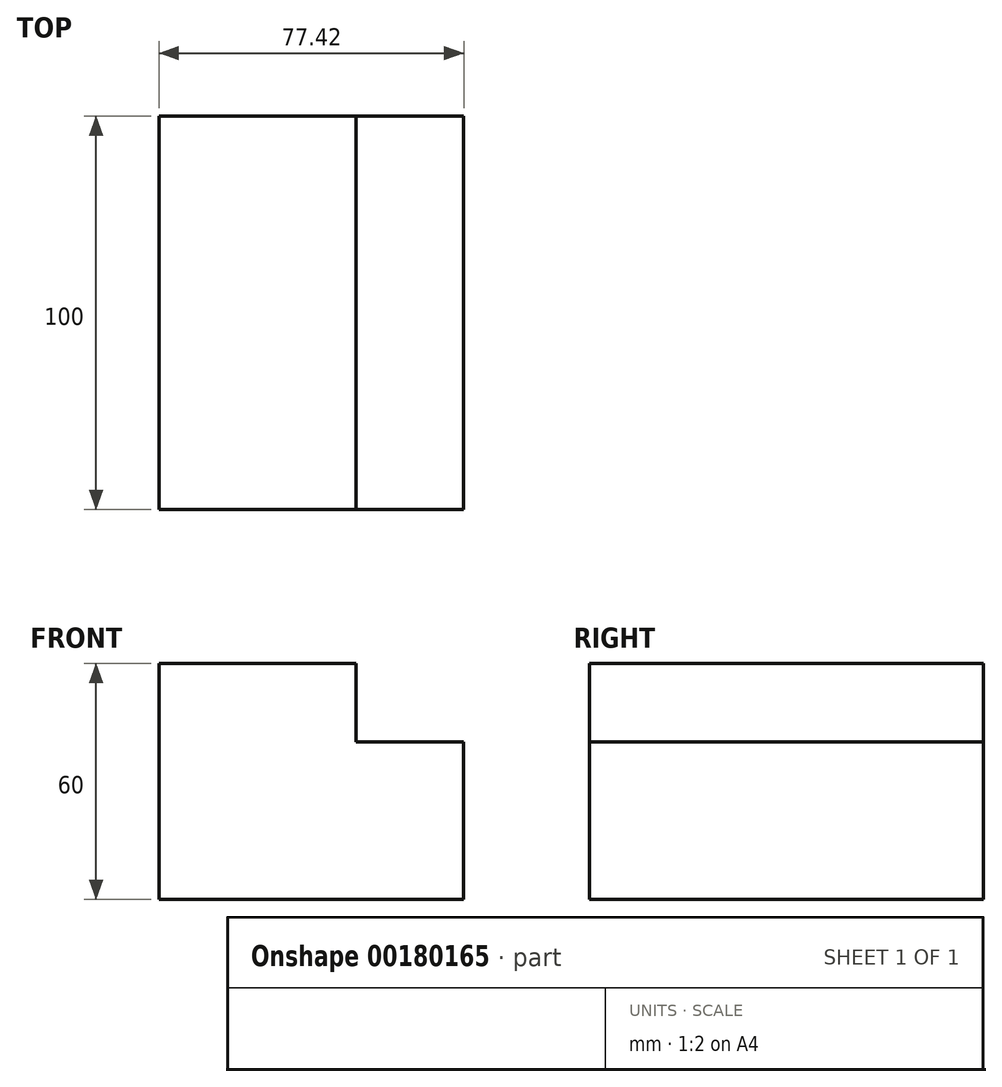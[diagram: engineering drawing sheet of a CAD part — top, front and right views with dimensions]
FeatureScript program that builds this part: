
annotation { "Feature Type Name" : "Feature", "Feature Type Description" : "" }
export const myFeature = defineFeature(function(context is Context, id is Id, definition is map)
    precondition{}
    {
        {
            var Q0;
            Q0=qCreatedBy(makeId("Front.planeOp"),FACE);
            var sketch = newSketch(context, id + "F0", { "sketchPlane" : qUnion([Q0])});
            skLineSegment(sketch, "E0", {"start": v(22.83, 0) * mm, "end": v(22.83, -20) * mm});
            skLineSegment(sketch, "E1", {"start": v(22.83, -20) * mm, "end": v(50.25, -20) * mm});
            skLineSegment(sketch, "E2", {"start": v(50.25, -20) * mm, "end": v(50.25, -60) * mm});
            skLineSegment(sketch, "E3", {"start": v(50.25, -60) * mm, "end": v(-27.17, -60) * mm});
            skLineSegment(sketch, "E4", {"start": v(-27.17, -60) * mm, "end": v(-27.17, 0) * mm});
            skLineSegment(sketch, "E5", {"start": v(-27.17, 0) * mm, "end": v(22.83, 0) * mm});
            skSolve(sketch);
        }
        {
            var Q0;
            Q0=makeQuery(id+"F0.imprint","IMPRINT",FACE,{"disambiguationData":[TD([[makeQuery(id+"F0.imprint","IMPRINT",EDGE,{"derivedFrom":sQuery(id+"F0.wireOp",EDGE,"E0")}),-1.0]])]});
            extrude(context, id + "F1", {"entities" : qUnion([Q0]), "endBound" : BoundingType.SYMMETRIC, "depth" : 100 * mm});
        }
    });
